# Revit family: ASH_ArmitageShanks_Urinals_UrinalDivision_S612001 (ASH_Contour21_S6120_BIM_GB)
name_source: partatom
category: Plumbing Fixtures
revit_build: Autodesk Revit MEP 2012 (Build: 20110309_2315(x64)
units: mm (PartAtom-declared; Revit-internal decimal feet)

## types (1)
- S612001 - Urinal Division
    AreaUnits = millimeters
    Assembly Code = C1030200
    AssetType = Fixed
    BIMObjectName = ASH_ArmitageShanks_Urinals_UrinalDivision
    Brand = Armitage Shanks
    CWFU = 0
    ConnectionType = PLUMBING
    Default Elevation = 610 mm  [stored 2.00131 ft]
    Description = Urinal division with hanger & screw
    DurationUnit = year
    ECA = No
    ExpectedLife = 30
    Features = Urinal division with hanger & screw
    Finish = White
    HWFU = 0
    IfcExportAs = IfcFurnitureType
    IfcExportType = USERDEFINED
    LinearUnits = millimeters
    MainColor = White
    ManufacturerURL = www.idealspec.co.uk
    Material = Vitreous china
    Model = S612001
    ModelNumber = S612001
    ModelReference = Urinal division with hanger & screw
    NBSDescription = Wall hung urinals
    NBSReference = 45-35-70/350
    Name = Urinals_UrinalDivision_ArmitageShanks
    NettWeight = 8.8 Kg
    NominalDepth = 320 mm  [stored 1.04987 ft]
    NominalHeight = 675 mm  [stored 2.21457 ft]
    NominalLength = 320 mm  [stored 1.04987 ft]
    NominalWidth = 130 mm  [stored 0.426509 ft]
    ProductInformation = www.idealspec.co.uk/datasheets/S612001
    Shape = Semi-Ellipse
    Size = 675 x 320 x 130 mm
    Space = Internal
    Style = Wall hung
    URL = www.idealspec.co.uk
    Uniclass2 = Pr_40_20_93_82
    Version = 2
    VolumeUnits = Litres
    WFU = 0
    WRAS = No
    WarrantyDescription = Manufacturers warranty
    WarrantyDurationParts = 99
    WarrantyDurationUnit = year
    WaterEfficientProduct = No

note: [stored X ft] marks values corroborated as IEEE doubles in the binary element streams (Revit-internal decimal feet)

## geometry (parser evidence)
native form markers: Blend x2, Sweep x3
no freeform markers — native parametric forms only
